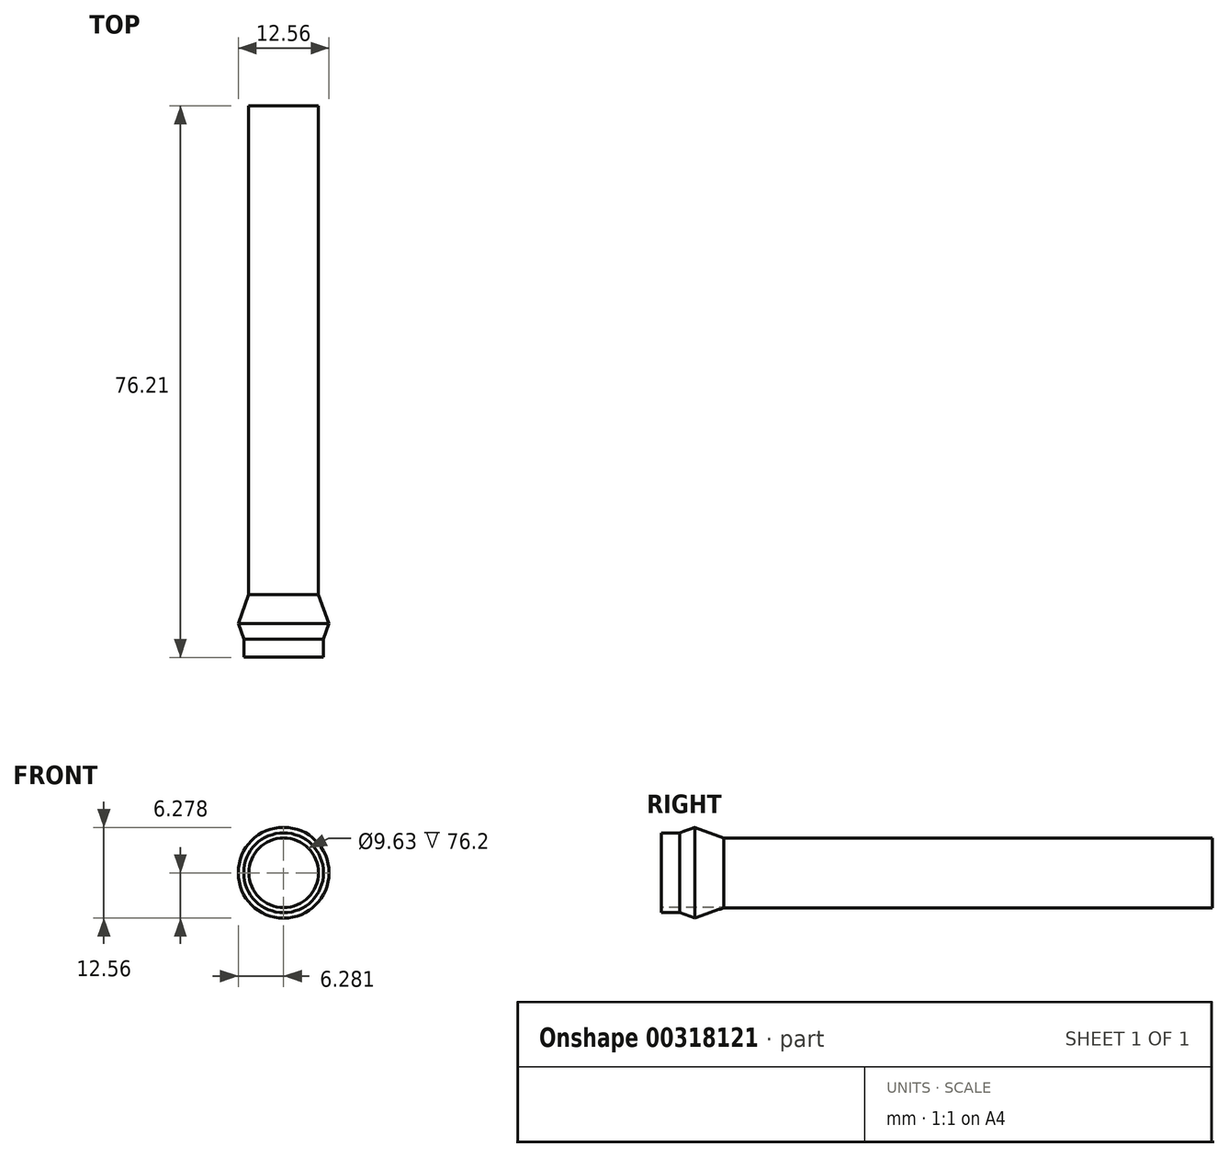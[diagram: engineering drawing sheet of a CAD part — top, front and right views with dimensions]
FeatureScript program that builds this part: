
annotation { "Feature Type Name" : "Feature", "Feature Type Description" : "" }
export const myFeature = defineFeature(function(context is Context, id is Id, definition is map)
    precondition{}
    {
        {
            var Q0;
            Q0=qCreatedBy(makeId("Front.planeOp"),FACE);
            var sketch = newSketch(context, id + "F0", { "sketchPlane" : qUnion([Q0])});
            skCircle(sketch, "E0", {"center": v(-45.97, 35.4) * mm, "radius": 6.35 * mm});
            skSolve(sketch);
        }
        {
            var Q0;
            Q0=makeQuery(id+"F0.imprint","IMPRINT",FACE,{"disambiguationData":[TD([[makeQuery(id+"F0.imprint","IMPRINT",EDGE,{"derivedFrom":sQuery(id+"F0.wireOp",EDGE,"E0")}),1.0]])]});
            extrude(context, id + "F1", {"entities" : qUnion([Q0]), "depth" : 8.9 * mm});
        }
        {
            var Q0;
            Q0=makeQuery(id+"F1.opExtrude","CAP_FACE",FACE,{"disambiguationData":[OSD([sQuery(id+"F0.wireOp",EDGE,"E0")])],"isStart":true});
            var sketch = newSketch(context, id + "F2", { "sketchPlane" : qUnion([Q0])});
            skCircle(sketch, "E1", {"center": v(45.97, 35.4) * mm, "radius": 4.83 * mm});
            skSolve(sketch);
        }
        {
            var Q0;
            Q0=makeQuery(id+"F2.imprint","IMPRINT",FACE,{"disambiguationData":[TD([[makeQuery(id+"F2.imprint","IMPRINT",EDGE,{"derivedFrom":sQuery(id+"F2.wireOp",EDGE,"E1")}),1.0]])]});
            extrude(context, id + "F3", {"entities" : qUnion([Q0]), "operationType" : NewBodyOperationType.ADD, "depth" : 66.67 * mm});
        }
        {
            var Q0;
            Q0=makeQuery(id+"F1.opExtrude","CAP_FACE",FACE,{"disambiguationData":[OSD([sQuery(id+"F0.wireOp",EDGE,"E0")])],"isStart":false});
            var sketch = newSketch(context, id + "F4", { "sketchPlane" : qUnion([Q0])});
            skPoint(sketch, "E2", {"position": v(-45.97, 35.4) * mm});
            skSolve(sketch);
        }
        {
            var Q0;
            Q0=sQuery(id+"F4.wireOp",VERTEX,"E2");
            var Q1;
            Q1=makeQuery(id+"F1.opExtrude","SWEPT_BODY",BODY,{"disambiguationData":[OSD([sQuery(id+"F0.wireOp",EDGE,"E0")])]});
            hole(context, id + "F5", {"style" : HoleStyle.SIMPLE, "endStyle" : HoleEndStyle.THROUGH, "holeDiameter" : 9.63 * mm, "tappedDepth" : 12.7 * mm, "tapClearance" : 3, "locations" : qUnion([Q0]), "scope" : qUnion([Q1])});
        }
        {
            var Q0;
            Q0=makeQuery(id+"F1.opExtrude","CAP_FACE",FACE,{"disambiguationData":[OSD([sQuery(id+"F0.wireOp",EDGE,"E0")])],"isStart":false});
            var sketch = newSketch(context, id + "F6", { "sketchPlane" : qUnion([Q0])});
            skCircle(sketch, "E3", {"center": v(-45.97, 35.4) * mm, "radius": 5.52 * mm});
            skSolve(sketch);
        }
        {
            var Q0;
            Q0=makeQuery(id+"F6.imprint","IMPRINT",FACE,{"disambiguationData":[TD([[makeQuery(id+"F6.imprint","IMPRINT",EDGE,{"derivedFrom":sQuery(id+"F6.wireOp",EDGE,"E3")}),1.0]])]});
            extrude(context, id + "F7", {"entities" : qUnion([Q0]), "operationType" : NewBodyOperationType.ADD, "depth" : 0.64 * mm});
        }
        {
            var Q0;
            Q0=makeQuery(id+"F1.opExtrude","CAP_EDGE",EDGE,{"disambiguationData":[OSD([sQuery(id+"F0.wireOp",EDGE,"E0")])],"isStart":false});
            chamfer(context, id + "F8", {"entities" : qUnion([Q0]), "chamferType" : ChamferType.OFFSET_ANGLE, "width" : 1.52 * mm, "oppositeDirection" : false, "angle" : 70 * degree, "tangentPropagation" : true});
        }
        {
            var Q0;
            Q0=makeQuery(id+"F1.opExtrude","CAP_EDGE",EDGE,{"disambiguationData":[OSD([sQuery(id+"F0.wireOp",EDGE,"E0")])],"isStart":true});
            chamfer(context, id + "F9", {"entities" : qUnion([Q0]), "chamferType" : ChamferType.OFFSET_ANGLE, "width" : 5.08 * mm, "oppositeDirection" : false, "angle" : 20 * degree, "tangentPropagation" : true});
        }
    });
